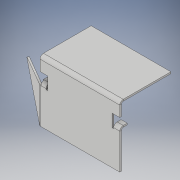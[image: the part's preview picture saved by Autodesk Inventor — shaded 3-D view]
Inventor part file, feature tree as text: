
AUTODESK INVENTOR PART (.ipt)
format: ipt  version: 2019 (Build 230136000, 136)  size: 247,808 bytes
history: native  units: in
note: dims shown in document units (in); Inventor stores cm internally (conversion verified against a paired STEP export)
features: sheet_metal_op x17, other x9, sketch x7
ambient origin geometry x8: Origin, YZ Plane, XZ Plane, XY Plane, X Axis, Y Axis, Z Axis, Center Point
bodies: Solid1 (feature_tree)
feature tree (33):
  sheet_metal_op  "Face1"
  sheet_metal_op  "Face2"
  sheet_metal_op  "Flange2"
  sheet_metal_op  "Flange3"
  sheet_metal_op  "Flange4"
  other  "Corner Chamfer1"
  sheet_metal_op  "Face3"
  sheet_metal_op  "Flange5"
  sketch  "Sketch1"  dims[d0=5.65in]
  other  "Plate1"
  sketch  "Sketch2"  dims[d1=2.75in]
  other  "Plate2"
  sheet_metal_op  "Bend1"
  sketch  "Sketch4"  dims[d2=0.12in]
  other  "Plate4"
  sheet_metal_op  "Bend3"
  sheet_metal_op  "Corner2"
  sketch  "Sketch5"  dims[d3=0.55in]
  other  "Plate5"
  sheet_metal_op  "Bend4"
  sheet_metal_op  "Corner3"
  sketch  "Sketch6"  dims[d4=0.55in]
  other  "Plate6"
  sheet_metal_op  "Bend5"
  sheet_metal_op  "Corner4"
  sketch  "Sketch7"  dims[d5=0.6in]
  other  "Plate7"
  sheet_metal_op  "Bend6"
  sketch  "Sketch8"  dims[d6=0.12in d7=0.12in d8=0.06in d9=0.24in d10=0.12in d21=0.12in d22=0.06in d23=0.24in d24=0.12in d25=0.4in d26=90.0deg d27=0.12in d28=0.48in d29=0.12in d30=0.12in d31=0.12in d32=0.06in d33=0.24in d34=0.12in d35=0.4in d36=90.0deg d37=0.12in d38=0.48in d39=0.12in d40=0.12in d41=0.12in d42=0.06in d43=0.24in d44=0.12in d45=2.5in d46=30.0deg d47=0.12in d48=0.48in d49=0.12in d50=0.12in d51=2.45in d52=0.25in d53=45.0deg d54=0.0in d55=5.65in d56=1.0in d57=0.12in d58=0.12in d59=0.06in d60=0.24in d61=0.12in d62=0.12in d63=0.06in d64=0.24in d65=0.12in d66=3.5in d67=90.0deg d68=0.12in d69=0.48in d70=0.12in d71=0.12in]
  other  "Plate8"
  sheet_metal_op  "Bend7"
  sheet_metal_op  "Corner5"
  other  "Definition1"
